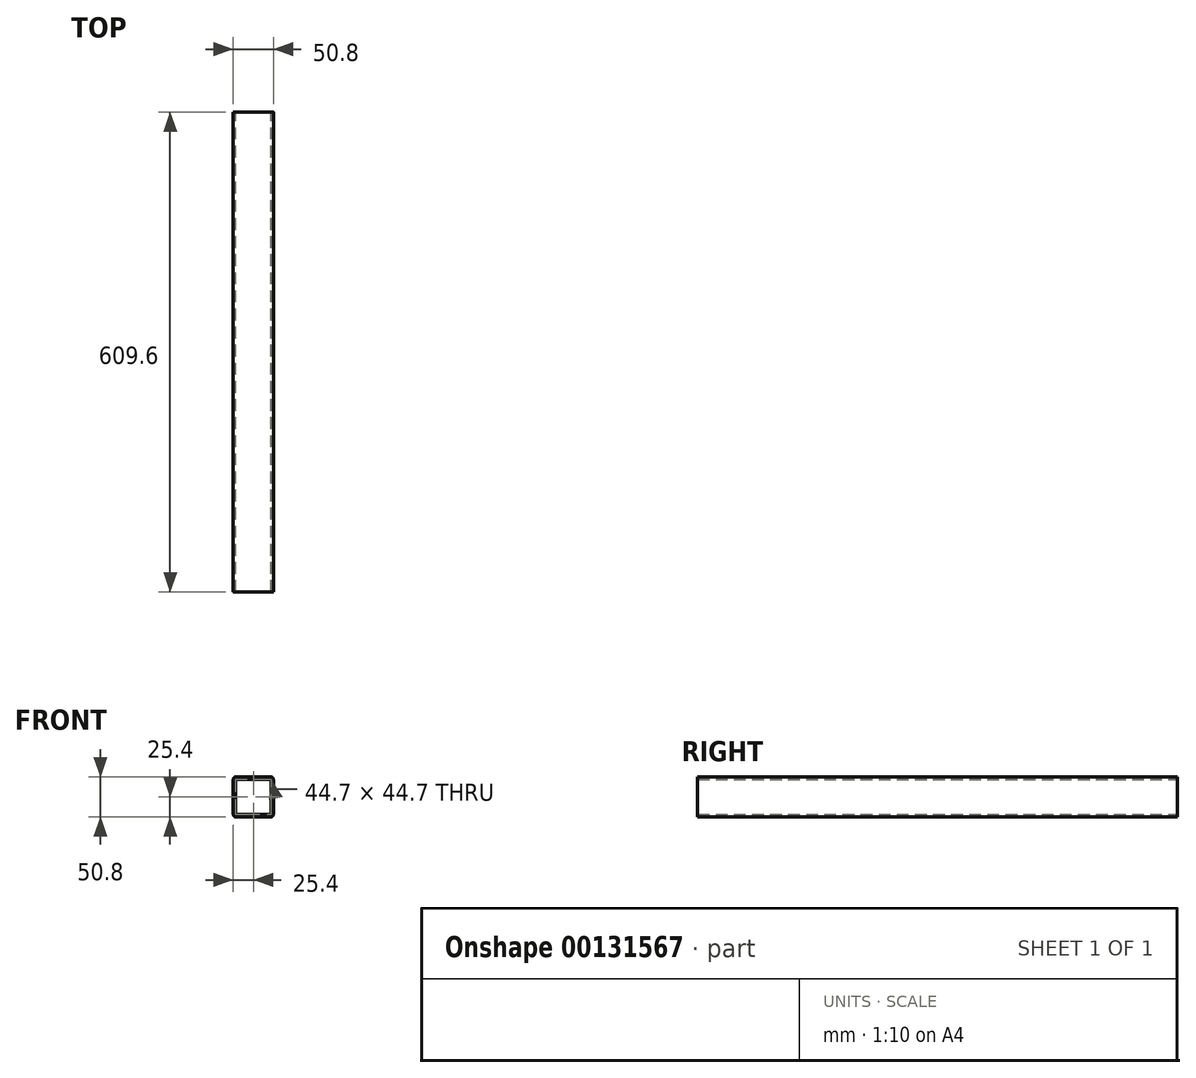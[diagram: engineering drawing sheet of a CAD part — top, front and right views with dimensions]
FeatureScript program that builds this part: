
annotation { "Feature Type Name" : "Feature", "Feature Type Description" : "" }
export const myFeature = defineFeature(function(context is Context, id is Id, definition is map)
    precondition{}
    {
        {
            var Q0;
            Q0=qCreatedBy(makeId("Front.planeOp"),FACE);
            var sketch = newSketch(context, id + "F0", { "sketchPlane" : qUnion([Q0])});
            skLineSegment(sketch, "E0.bottom", {"start": v(0, 0) * mm, "end": v(0, 0) * mm});
            skLineSegment(sketch, "E0.top", {"start": v(0, 0) * mm, "end": v(0, 0) * mm});
            skLineSegment(sketch, "E0.left", {"start": v(0, 0) * mm, "end": v(0, 0) * mm});
            skLineSegment(sketch, "E0.right", {"start": v(0, 0) * mm, "end": v(0, 0) * mm});
            skPoint(sketch, "E0.middle", {"position": v(0, 0) * mm});
            skLineSegment(sketch, "E1.bottom", {"start": v(22.35, 25.4) * mm, "end": v(-22.35, 25.4) * mm});
            skLineSegment(sketch, "E1.top", {"start": v(22.35, -25.4) * mm, "end": v(-22.35, -25.4) * mm});
            skLineSegment(sketch, "E1.left", {"start": v(25.4, 22.35) * mm, "end": v(25.4, -22.35) * mm});
            skLineSegment(sketch, "E1.right", {"start": v(-25.4, 22.35) * mm, "end": v(-25.4, -22.35) * mm});
            skLineSegment(sketch, "E2.bottom", {"start": v(22.35, 22.35) * mm, "end": v(-22.35, 22.35) * mm});
            skLineSegment(sketch, "E2.top", {"start": v(22.35, -22.35) * mm, "end": v(-22.35, -22.35) * mm});
            skLineSegment(sketch, "E2.left", {"start": v(22.35, 22.35) * mm, "end": v(22.35, -22.35) * mm});
            skLineSegment(sketch, "E2.right", {"start": v(-22.35, 22.35) * mm, "end": v(-22.35, -22.35) * mm});
            skPoint(sketch, "E3.visualSharp", {"position": v(-25.4, 25.4) * mm});
            skArc(sketch, "E3.filletArc", {"start": v(-22.35, 25.4) * mm, "mid": v(-24.5, 24.5) * mm, "end": v(-25.4, 22.35) * mm});
            skPoint(sketch, "E4.visualSharp", {"position": v(25.4, 25.4) * mm});
            skArc(sketch, "E4.filletArc", {"start": v(25.4, 22.35) * mm, "mid": v(24.5, 24.5) * mm, "end": v(22.35, 25.4) * mm});
            skPoint(sketch, "E5.visualSharp", {"position": v(25.4, -25.4) * mm});
            skArc(sketch, "E5.filletArc", {"start": v(22.35, -25.4) * mm, "mid": v(24.5, -24.5) * mm, "end": v(25.4, -22.35) * mm});
            skPoint(sketch, "E6.visualSharp", {"position": v(-25.4, -25.4) * mm});
            skArc(sketch, "E6.filletArc", {"start": v(-25.4, -22.35) * mm, "mid": v(-24.5, -24.5) * mm, "end": v(-22.35, -25.4) * mm});
            skSolve(sketch);
        }
        {
            var Q0;
            Q0=makeQuery(id+"F0.imprint","IMPRINT",FACE,{"disambiguationData":[TD([[makeQuery(id+"F0.imprint","IMPRINT",EDGE,{"derivedFrom":sQuery(id+"F0.wireOp",EDGE,"E1.bottom")}),1.0]])]});
            extrude(context, id + "F1", {"entities" : qUnion([Q0]), "depth" : 609.6 * mm});
        }
    });
